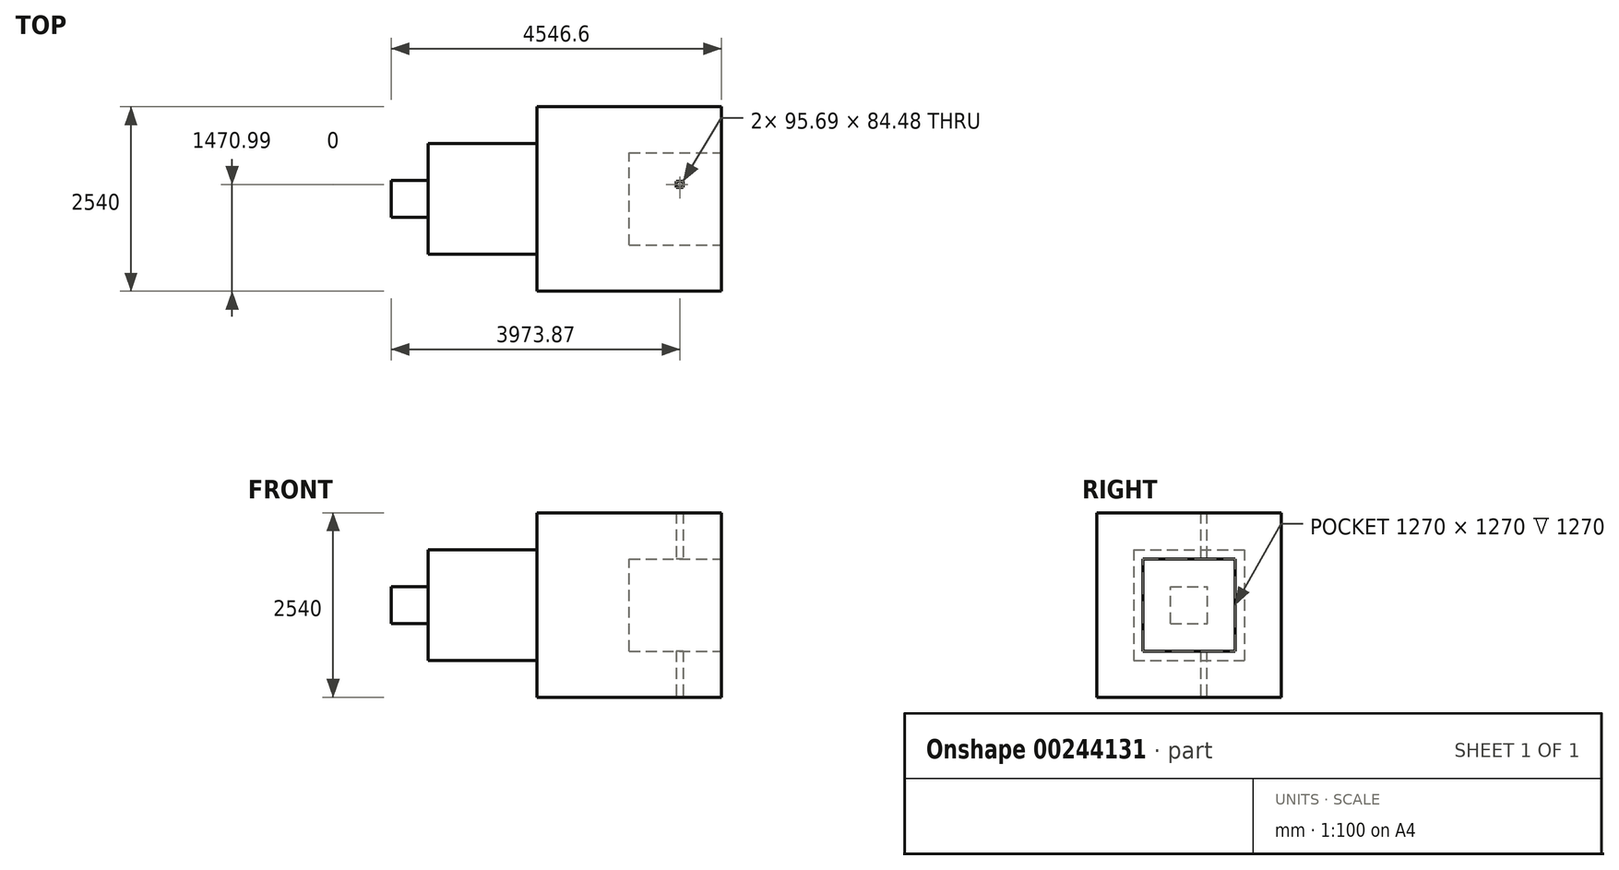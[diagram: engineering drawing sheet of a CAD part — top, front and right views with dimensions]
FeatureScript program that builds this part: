
annotation { "Feature Type Name" : "Feature", "Feature Type Description" : "" }
export const myFeature = defineFeature(function(context is Context, id is Id, definition is map)
    precondition{}
    {
        {
            var Q0;
            Q0=qCreatedBy(makeId("Top.planeOp"),FACE);
            var sketch = newSketch(context, id + "F0", { "sketchPlane" : qUnion([Q0])});
            skLineSegment(sketch, "E0.bottom", {"start": v(-1967.78, 1072.35) * mm, "end": v(572.22, 1072.35) * mm});
            skLineSegment(sketch, "E0.top", {"start": v(-1967.78, -1467.65) * mm, "end": v(572.22, -1467.65) * mm});
            skLineSegment(sketch, "E0.left", {"start": v(-1967.78, 1072.35) * mm, "end": v(-1967.78, -1467.65) * mm});
            skLineSegment(sketch, "E0.right", {"start": v(572.22, 1072.35) * mm, "end": v(572.22, -1467.65) * mm});
            skLineSegment(sketch, "E1.bottom", {"start": v(-48.35, 45.59) * mm, "end": v(47.34, 45.59) * mm});
            skLineSegment(sketch, "E1.top", {"start": v(-48.35, -38.9) * mm, "end": v(47.34, -38.9) * mm});
            skLineSegment(sketch, "E1.left", {"start": v(-48.35, 45.59) * mm, "end": v(-48.35, -38.9) * mm});
            skLineSegment(sketch, "E1.right", {"start": v(47.34, 45.59) * mm, "end": v(47.34, -38.9) * mm});
            skSolve(sketch);
        }
        {
            var Q0;
            Q0 = qSketchRegion(id + "F0", true);
            extrude(context, id + "F1", {"entities" : qUnion([Q0]), "depth" : 2540 * mm});
        }
        {
            var Q0;
            Q0=makeQuery(id+"F1.opExtrude","SWEPT_FACE",FACE,{"disambiguationData":[OSD([sQuery(id+"F0.wireOp",EDGE,"E0.left")])]});
            var sketch = newSketch(context, id + "F2", { "sketchPlane" : qUnion([Q0])});
            skLineSegment(sketch, "E2.bottom", {"start": v(959.65, 2032) * mm, "end": v(-564.35, 2032) * mm});
            skLineSegment(sketch, "E2.top", {"start": v(959.65, 508) * mm, "end": v(-564.35, 508) * mm});
            skLineSegment(sketch, "E2.left", {"start": v(959.65, 2032) * mm, "end": v(959.65, 508) * mm});
            skLineSegment(sketch, "E2.right", {"start": v(-564.35, 2032) * mm, "end": v(-564.35, 508) * mm});
            skSolve(sketch);
        }
        {
            var Q0;
            Q0=makeQuery(id+"F2.imprint","IMPRINT",FACE,{"disambiguationData":[TD([[makeQuery(id+"F2.imprint","IMPRINT",EDGE,{"derivedFrom":sQuery(id+"F2.wireOp",EDGE,"E2.bottom")}),1.0]])]});
            extrude(context, id + "F3", {"entities" : qUnion([Q0]), "operationType" : NewBodyOperationType.ADD, "depth" : 1498.6 * mm});
        }
        {
            var Q0;
            Q0=makeQuery(id+"F3.opExtrude","CAP_FACE",FACE,{"disambiguationData":[OSD([sQuery(id+"F2.wireOp",EDGE,"E2.bottom"),sQuery(id+"F2.wireOp",EDGE,"E2.top"),sQuery(id+"F2.wireOp",EDGE,"E2.left"),sQuery(id+"F2.wireOp",EDGE,"E2.right")])],"isStart":false});
            var sketch = newSketch(context, id + "F4", { "sketchPlane" : qUnion([Q0])});
            skLineSegment(sketch, "E3.bottom", {"start": v(451.65, 1016) * mm, "end": v(-56.35, 1016) * mm});
            skLineSegment(sketch, "E3.top", {"start": v(451.65, 1524) * mm, "end": v(-56.35, 1524) * mm});
            skLineSegment(sketch, "E3.left", {"start": v(451.65, 1016) * mm, "end": v(451.65, 1524) * mm});
            skLineSegment(sketch, "E3.right", {"start": v(-56.35, 1016) * mm, "end": v(-56.35, 1524) * mm});
            skSolve(sketch);
        }
        {
            var Q0;
            Q0=makeQuery(id+"F4.imprint","IMPRINT",FACE,{"disambiguationData":[TD([[makeQuery(id+"F4.imprint","IMPRINT",EDGE,{"derivedFrom":sQuery(id+"F4.wireOp",EDGE,"E3.bottom")}),-1.0]])]});
            extrude(context, id + "F5", {"entities" : qUnion([Q0]), "operationType" : NewBodyOperationType.ADD, "depth" : 508 * mm});
        }
        {
            var Q0;
            Q0=makeQuery(id+"F1.opExtrude","SWEPT_FACE",FACE,{"disambiguationData":[OSD([sQuery(id+"F0.wireOp",EDGE,"E0.right")])]});
            var sketch = newSketch(context, id + "F6", { "sketchPlane" : qUnion([Q0])});
            skSolve(sketch);
        }
        {
            var Q0;
            {var subQ0=sQuery(id+"F0.wireOp",EDGE,"E0.right");Q0=makeQuery(id+"F6.imprint","IMPRINT",FACE,{"disambiguationData":[TD([[makeQuery(id+"F6.imprint","IMPRINT",EDGE,{"derivedFrom":makeQuery(id+"F1.opExtrude","CAP_EDGE",EDGE,{"disambiguationData":[OSD([subQ0])],"isStart":true})}),-1.0]])]});}
            var sketch = newSketch(context, id + "F7", { "sketchPlane" : qUnion([Q0])});
            skLineSegment(sketch, "E4.bottom", {"start": v(-832.65, 635) * mm, "end": v(437.35, 635) * mm});
            skLineSegment(sketch, "E4.top", {"start": v(-832.65, 1905) * mm, "end": v(437.35, 1905) * mm});
            skLineSegment(sketch, "E4.left", {"start": v(-832.65, 635) * mm, "end": v(-832.65, 1905) * mm});
            skLineSegment(sketch, "E4.right", {"start": v(437.35, 635) * mm, "end": v(437.35, 1905) * mm});
            skSolve(sketch);
        }
        {
            var Q0;
            Q0 = qSketchRegion(id + "F7", true);
            extrude(context, id + "F8", {"entities" : qUnion([Q0]), "operationType" : NewBodyOperationType.REMOVE, "oppositeDirection" : true, "depth" : 1270 * mm});
        }
    });
